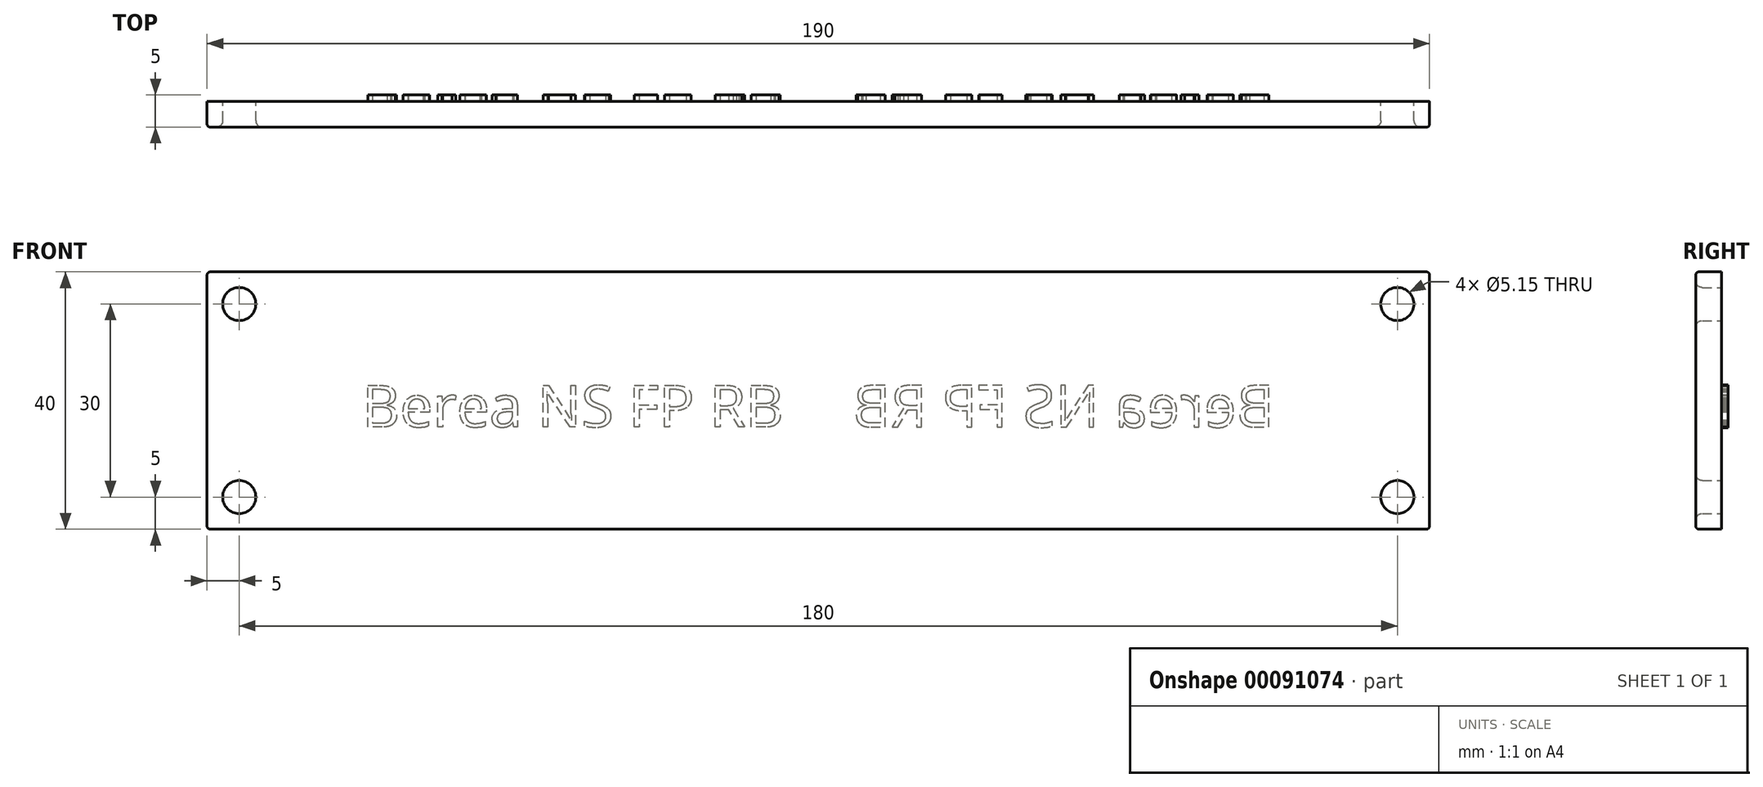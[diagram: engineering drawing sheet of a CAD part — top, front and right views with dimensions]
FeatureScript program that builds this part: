
annotation { "Feature Type Name" : "Feature", "Feature Type Description" : "" }
export const myFeature = defineFeature(function(context is Context, id is Id, definition is map)
    precondition{}
    {
        {
            var Q0;
            Q0=qCreatedBy(makeId("Front.planeOp"),FACE);
            var sketch = newSketch(context, id + "F0", { "sketchPlane" : qUnion([Q0])});
            skLineSegment(sketch, "E0.bottom", {"start": v(-95, -20) * mm, "end": v(95, -20) * mm});
            skLineSegment(sketch, "E0.top", {"start": v(-95, 20) * mm, "end": v(95, 20) * mm});
            skLineSegment(sketch, "E0.left", {"start": v(-95, -20) * mm, "end": v(-95, 20) * mm});
            skLineSegment(sketch, "E0.right", {"start": v(95, -20) * mm, "end": v(95, 20) * mm});
            skPoint(sketch, "E0.middle", {"position": v(0, 0) * mm});
            skCircle(sketch, "E1", {"center": v(-90, 15) * mm, "radius": 2.58 * mm});
            skPoint(sketch, "E2.start.orphan", {"position": v(-95, 0) * mm});
            skPoint(sketch, "E3.orphan", {"position": v(0, 20) * mm});
            skPoint(sketch, "E4.end.orphan", {"position": v(0, -20) * mm});
            skLineSegment(sketch, "E5", {"start": v(-95, 0) * mm, "end": v(0, 0) * mm, "construction": true});
            skLineSegment(sketch, "E6", {"start": v(0, 20) * mm, "end": v(0, -20) * mm, "construction": true});
            skCircle(sketch, "E7.MirrorC", {"center": v(-90, -15) * mm, "radius": 2.58 * mm});
            skCircle(sketch, "E8.MirrorC", {"center": v(90, 15) * mm, "radius": 2.58 * mm});
            skCircle(sketch, "E9.MirrorC", {"center": v(90, -15) * mm, "radius": 2.58 * mm});
            skSolve(sketch);
        }
        {
            var Q0;
            Q0=makeQuery(id+"F0.imprint","IMPRINT",FACE,{"disambiguationData":[TD([[makeQuery(id+"F0.imprint","IMPRINT",EDGE,{"derivedFrom":sQuery(id+"F0.wireOp",EDGE,"E0.bottom")}),1.0]])]});
            extrude(context, id + "F1", {"entities" : qUnion([Q0]), "depth" : 4 * mm});
        }
        {
            var Q0;
            Q0=makeQuery(id+"F1.opExtrude","CAP_EDGE",EDGE,{"disambiguationData":[OSD([sQuery(id+"F0.wireOp",EDGE,"E1")])],"isStart":false});
            var Q1;
            Q1=makeQuery(id+"F1.opExtrude","CAP_EDGE",EDGE,{"disambiguationData":[OSD([sQuery(id+"F0.wireOp",EDGE,"f5b72a5b-8583-449a-bdbf-9ac5a681e1fd0.MirrorC")])],"isStart":false});
            var Q2;
            Q2=makeQuery(id+"F1.opExtrude","CAP_EDGE",EDGE,{"disambiguationData":[OSD([sQuery(id+"F0.wireOp",EDGE,"2623e306-60f4-4522-aa65-1e3e8c2cf5b60.MirrorC")])],"isStart":false});
            var Q3;
            Q3=makeQuery(id+"F1.opExtrude","CAP_EDGE",EDGE,{"disambiguationData":[OSD([sQuery(id+"F0.wireOp",EDGE,"be81a34d-1d50-4ce7-a7a8-4484a1701fac0.MirrorC")])],"isStart":false});
            var Q4;
            Q4=makeQuery(id+"F1.opExtrude","CAP_EDGE",EDGE,{"disambiguationData":[OSD([sQuery(id+"F0.wireOp",EDGE,"E7.MirrorC")])],"isStart":false});
            var Q5;
            Q5=makeQuery(id+"F1.opExtrude","CAP_EDGE",EDGE,{"disambiguationData":[OSD([sQuery(id+"F0.wireOp",EDGE,"E8.MirrorC")])],"isStart":false});
            var Q6;
            Q6=makeQuery(id+"F1.opExtrude","CAP_EDGE",EDGE,{"disambiguationData":[OSD([sQuery(id+"F0.wireOp",EDGE,"E9.MirrorC")])],"isStart":false});
            fillet(context, id + "F2", {"entities" : qUnion([Q0, Q1, Q2, Q3, Q4, Q5, Q6]), "radius" : 1 * mm, "tangentPropagation" : true, "allowEdgeOverflow" : false});
        }
        {
            var Q0;
            Q0=makeQuery(id+"F1.opExtrude","CAP_EDGE",EDGE,{"disambiguationData":[OSD([sQuery(id+"F0.wireOp",EDGE,"E0.top")])],"isStart":false});
            var Q1;
            Q1=makeQuery(id+"F1.opExtrude","CAP_EDGE",EDGE,{"disambiguationData":[OSD([sQuery(id+"F0.wireOp",EDGE,"E0.left")])],"isStart":false});
            var Q2;
            Q2=makeQuery(id+"F1.opExtrude","CAP_EDGE",EDGE,{"disambiguationData":[OSD([sQuery(id+"F0.wireOp",EDGE,"E0.bottom")])],"isStart":false});
            var Q3;
            Q3=makeQuery(id+"F1.opExtrude","CAP_EDGE",EDGE,{"disambiguationData":[OSD([sQuery(id+"F0.wireOp",EDGE,"E0.right")])],"isStart":false});
            var Q4;
            Q4=makeQuery(id+"F1.opExtrude","SWEPT_EDGE",EDGE,{"disambiguationData":[OSD([sQuery(id+"F0.wireOp",EDGE,"E0.top"),sQuery(id+"F0.wireOp",EDGE,"E0.left")])]});
            var Q5;
            Q5=makeQuery(id+"F1.opExtrude","SWEPT_EDGE",EDGE,{"disambiguationData":[OSD([sQuery(id+"F0.wireOp",EDGE,"E0.bottom"),sQuery(id+"F0.wireOp",EDGE,"E0.left")])]});
            var Q6;
            Q6=makeQuery(id+"F1.opExtrude","SWEPT_EDGE",EDGE,{"disambiguationData":[OSD([sQuery(id+"F0.wireOp",EDGE,"E0.top"),sQuery(id+"F0.wireOp",EDGE,"E0.right")])]});
            var Q7;
            Q7=makeQuery(id+"F1.opExtrude","SWEPT_EDGE",EDGE,{"disambiguationData":[OSD([sQuery(id+"F0.wireOp",EDGE,"E0.bottom"),sQuery(id+"F0.wireOp",EDGE,"E0.right")])]});
            fillet(context, id + "F3", {"entities" : qUnion([Q0, Q1, Q2, Q3, Q4, Q5, Q6, Q7]), "radius" : .5 * mm, "tangentPropagation" : true, "allowEdgeOverflow" : false});
        }
        {
            var Q0;
            Q0=makeQuery(id+"F1.opExtrude","CAP_FACE",FACE,{"disambiguationData":[OSD([sQuery(id+"F0.wireOp",EDGE,"E0.bottom"),sQuery(id+"F0.wireOp",EDGE,"E0.top"),sQuery(id+"F0.wireOp",EDGE,"E0.left"),sQuery(id+"F0.wireOp",EDGE,"E0.right"),sQuery(id+"F0.wireOp",EDGE,"E1"),sQuery(id+"F0.wireOp",EDGE,"E7.MirrorC"),sQuery(id+"F0.wireOp",EDGE,"E8.MirrorC"),sQuery(id+"F0.wireOp",EDGE,"E9.MirrorC")])],"isStart":true});
            var sketch = newSketch(context, id + "F4", { "sketchPlane" : qUnion([Q0])});
            skText(sketch, "E10", { "text": "Berea NS FP RB\n", "fontName": "OpenSans-Regular.ttf"});
            skLineSegment(sketch, "E11", {"start": v(0, 20) * mm, "end": v(0, -20) * mm, "construction": true});
            const initialGuessF4  = {"E10": [-0.07092, -0.00413, 1, 0, 0.00655]};
            skSetInitialGuess(sketch, initialGuessF4);
            skSolve(sketch);
        }
        {
            var Q0;
            Q0=qSketchRegion(id+"F4",true);
            extrude(context, id + "F5", {"entities" : qUnion([Q0]), "operationType" : NewBodyOperationType.ADD, "flatOperationType" : FlatOperationType.REMOVE, "offsetDistance" : 25 * mm, "depth" : 1 * mm, "domain" : OperationDomain.MODEL});
        }
        {
            var Q0;
            Q0=makeQuery(id+"F1.opExtrude","SWEPT_BODY",BODY,{"disambiguationData":[OSD([sQuery(id+"F0.wireOp",EDGE,"E0.bottom"),sQuery(id+"F0.wireOp",EDGE,"E0.top"),sQuery(id+"F0.wireOp",EDGE,"E0.left"),sQuery(id+"F0.wireOp",EDGE,"E0.right"),sQuery(id+"F0.wireOp",EDGE,"E1"),sQuery(id+"F0.wireOp",EDGE,"E7.MirrorC"),sQuery(id+"F0.wireOp",EDGE,"E8.MirrorC"),sQuery(id+"F0.wireOp",EDGE,"E9.MirrorC")])]});
            var Q1;
            Q1=makeQuery(id+"F5.opExtrude","SWEPT_FACE",FACE,{"disambiguationData":[OSD([sQuery(id+"F4.wireOp",EDGE,"E10.sketch_text.stroke-94")])]});
            var Q2;
            Q2=makeQuery(id+"F5.opExtrude","SWEPT_FACE",FACE,{"disambiguationData":[OSD([sQuery(id+"F4.wireOp",EDGE,"E10.sketch_text.stroke-169")])]});
            var Q3;
            Q3=makeQuery(id+"F5.opExtrude","SWEPT_FACE",FACE,{"disambiguationData":[OSD([sQuery(id+"F4.wireOp",EDGE,"E10.sketch_text.stroke-185")])]});
            var Q4;
            Q4=makeQuery(id+"F5.opExtrude","SWEPT_FACE",FACE,{"disambiguationData":[OSD([sQuery(id+"F4.wireOp",EDGE,"E10.sketch_text.stroke-125")])]});
            var Q5;
            Q5=makeQuery(id+"F5.opExtrude","SWEPT_FACE",FACE,{"disambiguationData":[OSD([sQuery(id+"F4.wireOp",EDGE,"E10.sketch_text.stroke-155")])]});
            var Q6;
            Q6=makeQuery(id+"F5.opExtrude","SWEPT_FACE",FACE,{"disambiguationData":[OSD([sQuery(id+"F4.wireOp",EDGE,"E10.sketch_text.stroke-65")])]});
            var Q7;
            Q7=makeQuery(id+"F5.opExtrude","SWEPT_FACE",FACE,{"disambiguationData":[OSD([sQuery(id+"F4.wireOp",EDGE,"E10.sketch_text.stroke-81")])]});
            var Q8;
            Q8=makeQuery(id+"F5.opExtrude","SWEPT_FACE",FACE,{"disambiguationData":[OSD([sQuery(id+"F4.wireOp",EDGE,"E10.sketch_text.stroke-67")])]});
            var Q9;
            Q9=makeQuery(id+"F5.opExtrude","SWEPT_FACE",FACE,{"disambiguationData":[OSD([sQuery(id+"F4.wireOp",EDGE,"E10.sketch_text.stroke-99")])]});
            var Q10;
            Q10=makeQuery(id+"F5.opExtrude","SWEPT_FACE",FACE,{"disambiguationData":[OSD([sQuery(id+"F4.wireOp",EDGE,"E10.sketch_text.stroke-127")])]});
            var Q11;
            Q11=makeQuery(id+"F5.opExtrude","SWEPT_FACE",FACE,{"disambiguationData":[OSD([sQuery(id+"F4.wireOp",EDGE,"E10.sketch_text.stroke-10")])]});
            var Q12;
            Q12=makeQuery(id+"F5.opExtrude","CAP_FACE",FACE,{"disambiguationData":[OSD([sQuery(id+"F4.wireOp",EDGE,"E10.sketch_text.stroke-9"),sQuery(id+"F4.wireOp",EDGE,"E10.sketch_text.stroke-10"),sQuery(id+"F4.wireOp",EDGE,"E10.sketch_text.stroke-11"),sQuery(id+"F4.wireOp",EDGE,"E10.sketch_text.stroke-12")])],"isStart":false});
            var Q13;
            Q13=makeQuery(id+"F5.opExtrude","SWEPT_FACE",FACE,{"disambiguationData":[OSD([sQuery(id+"F4.wireOp",EDGE,"E10.sketch_text.stroke-154")])]});
            var Q14;
            Q14=makeQuery(id+"F5.opExtrude","SWEPT_FACE",FACE,{"disambiguationData":[OSD([sQuery(id+"F4.wireOp",EDGE,"E10.sketch_text.stroke-1")])]});
            var Q15;
            Q15=makeQuery(id+"F5.opExtrude","CAP_FACE",FACE,{"disambiguationData":[OSD([sQuery(id+"F4.wireOp",EDGE,"E10.sketch_text.stroke-124"),sQuery(id+"F4.wireOp",EDGE,"E10.sketch_text.stroke-125"),sQuery(id+"F4.wireOp",EDGE,"E10.sketch_text.stroke-126"),sQuery(id+"F4.wireOp",EDGE,"E10.sketch_text.stroke-127"),sQuery(id+"F4.wireOp",EDGE,"E10.sketch_text.stroke-128"),sQuery(id+"F4.wireOp",EDGE,"E10.sketch_text.stroke-129"),sQuery(id+"F4.wireOp",EDGE,"E10.sketch_text.stroke-130"),sQuery(id+"F4.wireOp",EDGE,"E10.sketch_text.stroke-131"),sQuery(id+"F4.wireOp",EDGE,"E10.sketch_text.stroke-132"),sQuery(id+"F4.wireOp",EDGE,"E10.sketch_text.stroke-133"),sQuery(id+"F4.wireOp",EDGE,"E10.sketch_text.stroke-134"),sQuery(id+"F4.wireOp",EDGE,"E10.sketch_text.stroke-135"),sQuery(id+"F4.wireOp",EDGE,"E10.sketch_text.stroke-136"),sQuery(id+"F4.wireOp",EDGE,"E10.sketch_text.stroke-137"),sQuery(id+"F4.wireOp",EDGE,"E10.sketch_text.stroke-138")])],"isStart":false});
            var Q16;
            Q16=makeQuery(id+"F5.opExtrude","CAP_FACE",FACE,{"disambiguationData":[OSD([sQuery(id+"F4.wireOp",EDGE,"E10.sketch_text.stroke-34"),sQuery(id+"F4.wireOp",EDGE,"E10.sketch_text.stroke-35"),sQuery(id+"F4.wireOp",EDGE,"E10.sketch_text.stroke-36"),sQuery(id+"F4.wireOp",EDGE,"E10.sketch_text.stroke-37"),sQuery(id+"F4.wireOp",EDGE,"E10.sketch_text.stroke-38"),sQuery(id+"F4.wireOp",EDGE,"E10.sketch_text.stroke-39"),sQuery(id+"F4.wireOp",EDGE,"E10.sketch_text.stroke-40"),sQuery(id+"F4.wireOp",EDGE,"E10.sketch_text.stroke-41"),sQuery(id+"F4.wireOp",EDGE,"E10.sketch_text.stroke-42"),sQuery(id+"F4.wireOp",EDGE,"E10.sketch_text.stroke-43"),sQuery(id+"F4.wireOp",EDGE,"E10.sketch_text.stroke-44"),sQuery(id+"F4.wireOp",EDGE,"E10.sketch_text.stroke-45"),sQuery(id+"F4.wireOp",EDGE,"E10.sketch_text.stroke-46"),sQuery(id+"F4.wireOp",EDGE,"E10.sketch_text.stroke-47"),sQuery(id+"F4.wireOp",EDGE,"E10.sketch_text.stroke-48"),sQuery(id+"F4.wireOp",EDGE,"E10.sketch_text.stroke-49"),sQuery(id+"F4.wireOp",EDGE,"E10.sketch_text.stroke-50"),sQuery(id+"F4.wireOp",EDGE,"E10.sketch_text.stroke-51"),sQuery(id+"F4.wireOp",EDGE,"E10.sketch_text.stroke-52"),sQuery(id+"F4.wireOp",EDGE,"E10.sketch_text.stroke-53"),sQuery(id+"F4.wireOp",EDGE,"E10.sketch_text.stroke-54"),sQuery(id+"F4.wireOp",EDGE,"E10.sketch_text.stroke-55"),sQuery(id+"F4.wireOp",EDGE,"E10.sketch_text.stroke-56"),sQuery(id+"F4.wireOp",EDGE,"E10.sketch_text.stroke-57"),sQuery(id+"F4.wireOp",EDGE,"E10.sketch_text.stroke-58"),sQuery(id+"F4.wireOp",EDGE,"E10.sketch_text.stroke-59"),sQuery(id+"F4.wireOp",EDGE,"E10.sketch_text.stroke-60")])],"isStart":false});
            var Q17;
            Q17=makeQuery(id+"F5.opExtrude","SWEPT_FACE",FACE,{"disambiguationData":[OSD([sQuery(id+"F4.wireOp",EDGE,"E10.sketch_text.stroke-50")])]});
            var Q18;
            Q18=makeQuery(id+"F5.opExtrude","SWEPT_FACE",FACE,{"disambiguationData":[OSD([sQuery(id+"F4.wireOp",EDGE,"E10.sketch_text.stroke-2")])]});
            var Q19;
            Q19=makeQuery(id+"F5.opExtrude","SWEPT_FACE",FACE,{"disambiguationData":[OSD([sQuery(id+"F4.wireOp",EDGE,"E10.sketch_text.stroke-3")])]});
            var Q20;
            Q20=makeQuery(id+"F5.opExtrude","SWEPT_FACE",FACE,{"disambiguationData":[OSD([sQuery(id+"F4.wireOp",EDGE,"E10.sketch_text.stroke-5")])]});
            var Q21;
            Q21=makeQuery(id+"F5.opExtrude","SWEPT_FACE",FACE,{"disambiguationData":[OSD([sQuery(id+"F4.wireOp",EDGE,"E10.sketch_text.stroke-8")])]});
            var Q22;
            Q22=makeQuery(id+"F5.opExtrude","SWEPT_FACE",FACE,{"disambiguationData":[OSD([sQuery(id+"F4.wireOp",EDGE,"E10.sketch_text.stroke-98")])]});
            var Q23;
            Q23=makeQuery(id+"F5.opExtrude","SWEPT_FACE",FACE,{"disambiguationData":[OSD([sQuery(id+"F4.wireOp",EDGE,"E10.sketch_text.stroke-66")])]});
            var Q24;
            Q24=makeQuery(id+"F5.opExtrude","SWEPT_FACE",FACE,{"disambiguationData":[OSD([sQuery(id+"F4.wireOp",EDGE,"E10.sketch_text.stroke-153")])]});
            var Q25;
            Q25=makeQuery(id+"F5.opExtrude","SWEPT_FACE",FACE,{"disambiguationData":[OSD([sQuery(id+"F4.wireOp",EDGE,"E10.sketch_text.stroke-126")])]});
            var Q26;
            Q26=makeQuery(id+"F5.opExtrude","SWEPT_FACE",FACE,{"disambiguationData":[OSD([sQuery(id+"F4.wireOp",EDGE,"E10.sketch_text.stroke-183")])]});
            var Q27;
            Q27=makeQuery(id+"F5.opExtrude","SWEPT_FACE",FACE,{"disambiguationData":[OSD([sQuery(id+"F4.wireOp",EDGE,"E10.sketch_text.stroke-109")])]});
            var Q28;
            Q28=makeQuery(id+"F5.opExtrude","SWEPT_FACE",FACE,{"disambiguationData":[OSD([sQuery(id+"F4.wireOp",EDGE,"E10.sketch_text.stroke-186")])]});
            var Q29;
            Q29=makeQuery(id+"F5.opExtrude","SWEPT_FACE",FACE,{"disambiguationData":[OSD([sQuery(id+"F4.wireOp",EDGE,"E10.sketch_text.stroke-79")])]});
            var Q30;
            Q30=makeQuery(id+"F5.opExtrude","SWEPT_FACE",FACE,{"disambiguationData":[OSD([sQuery(id+"F4.wireOp",EDGE,"E10.sketch_text.stroke-110")])]});
            var Q31;
            Q31=makeQuery(id+"F5.opExtrude","SWEPT_FACE",FACE,{"disambiguationData":[OSD([sQuery(id+"F4.wireOp",EDGE,"E10.sketch_text.stroke-38")])]});
            var Q32;
            Q32=makeQuery(id+"F5.opExtrude","SWEPT_FACE",FACE,{"disambiguationData":[OSD([sQuery(id+"F4.wireOp",EDGE,"E10.sketch_text.stroke-24")])]});
            var Q33;
            Q33=makeQuery(id+"F5.opExtrude","SWEPT_FACE",FACE,{"disambiguationData":[OSD([sQuery(id+"F4.wireOp",EDGE,"E10.sketch_text.stroke-12")])]});
            var Q34;
            Q34=makeQuery(id+"F5.opExtrude","SWEPT_FACE",FACE,{"disambiguationData":[OSD([sQuery(id+"F4.wireOp",EDGE,"E10.sketch_text.stroke-100")])]});
            var Q35;
            Q35=makeQuery(id+"F5.opExtrude","SWEPT_FACE",FACE,{"disambiguationData":[OSD([sQuery(id+"F4.wireOp",EDGE,"E10.sketch_text.stroke-158")])]});
            var Q36;
            Q36=makeQuery(id+"F5.opExtrude","SWEPT_FACE",FACE,{"disambiguationData":[OSD([sQuery(id+"F4.wireOp",EDGE,"E10.sketch_text.stroke-142")])]});
            var Q37;
            Q37=makeQuery(id+"F5.opExtrude","SWEPT_FACE",FACE,{"disambiguationData":[OSD([sQuery(id+"F4.wireOp",EDGE,"E10.sketch_text.stroke-54")])]});
            var Q38;
            Q38=makeQuery(id+"F5.opExtrude","SWEPT_FACE",FACE,{"disambiguationData":[OSD([sQuery(id+"F4.wireOp",EDGE,"E10.sketch_text.stroke-25")])]});
            var Q39;
            Q39=makeQuery(id+"F5.opExtrude","SWEPT_FACE",FACE,{"disambiguationData":[OSD([sQuery(id+"F4.wireOp",EDGE,"E10.sketch_text.stroke-101")])]});
            var Q40;
            Q40=makeQuery(id+"F5.opExtrude","SWEPT_FACE",FACE,{"disambiguationData":[OSD([sQuery(id+"F4.wireOp",EDGE,"E10.sketch_text.stroke-69")])]});
            var Q41;
            Q41=makeQuery(id+"F5.opExtrude","SWEPT_FACE",FACE,{"disambiguationData":[OSD([sQuery(id+"F4.wireOp",EDGE,"E10.sketch_text.stroke-159")])]});
            var Q42;
            Q42=makeQuery(id+"F5.opExtrude","SWEPT_FACE",FACE,{"disambiguationData":[OSD([sQuery(id+"F4.wireOp",EDGE,"E10.sketch_text.stroke-85")])]});
            var Q43;
            Q43=makeQuery(id+"F5.opExtrude","SWEPT_FACE",FACE,{"disambiguationData":[OSD([sQuery(id+"F4.wireOp",EDGE,"E10.sketch_text.stroke-173")])]});
            var Q44;
            Q44=makeQuery(id+"F5.opExtrude","SWEPT_FACE",FACE,{"disambiguationData":[OSD([sQuery(id+"F4.wireOp",EDGE,"E10.sketch_text.stroke-40")])]});
            var Q45;
            Q45=makeQuery(id+"F5.opExtrude","SWEPT_FACE",FACE,{"disambiguationData":[OSD([sQuery(id+"F4.wireOp",EDGE,"E10.sketch_text.stroke-102")])]});
            var Q46;
            Q46=makeQuery(id+"F5.opExtrude","SWEPT_FACE",FACE,{"disambiguationData":[OSD([sQuery(id+"F4.wireOp",EDGE,"E10.sketch_text.stroke-86")])]});
            var Q47;
            Q47=makeQuery(id+"F5.opExtrude","SWEPT_FACE",FACE,{"disambiguationData":[OSD([sQuery(id+"F4.wireOp",EDGE,"E10.sketch_text.stroke-130")])]});
            var Q48;
            Q48=makeQuery(id+"F5.opExtrude","SWEPT_FACE",FACE,{"disambiguationData":[OSD([sQuery(id+"F4.wireOp",EDGE,"E10.sketch_text.stroke-103")])]});
            var Q49;
            Q49=makeQuery(id+"F5.opExtrude","SWEPT_FACE",FACE,{"disambiguationData":[OSD([sQuery(id+"F4.wireOp",EDGE,"E10.sketch_text.stroke-87")])]});
            var Q50;
            Q50=makeQuery(id+"F5.opExtrude","SWEPT_FACE",FACE,{"disambiguationData":[OSD([sQuery(id+"F4.wireOp",EDGE,"E10.sketch_text.stroke-145")])]});
            var Q51;
            Q51=makeQuery(id+"F5.opExtrude","SWEPT_FACE",FACE,{"disambiguationData":[OSD([sQuery(id+"F4.wireOp",EDGE,"E10.sketch_text.stroke-131")])]});
            var Q52;
            Q52=makeQuery(id+"F5.opExtrude","SWEPT_FACE",FACE,{"disambiguationData":[OSD([sQuery(id+"F4.wireOp",EDGE,"E10.sketch_text.stroke-28")])]});
            var Q53;
            Q53=makeQuery(id+"F5.opExtrude","SWEPT_FACE",FACE,{"disambiguationData":[OSD([sQuery(id+"F4.wireOp",EDGE,"E10.sketch_text.stroke-14")])]});
            var Q54;
            Q54=makeQuery(id+"F5.opExtrude","SWEPT_FACE",FACE,{"disambiguationData":[OSD([sQuery(id+"F4.wireOp",EDGE,"E10.sketch_text.stroke-88")])]});
            var Q55;
            Q55=makeQuery(id+"F5.opExtrude","SWEPT_FACE",FACE,{"disambiguationData":[OSD([sQuery(id+"F4.wireOp",EDGE,"E10.sketch_text.stroke-162")])]});
            var Q56;
            Q56=makeQuery(id+"F5.opExtrude","SWEPT_FACE",FACE,{"disambiguationData":[OSD([sQuery(id+"F4.wireOp",EDGE,"E10.sketch_text.stroke-176")])]});
            var Q57;
            Q57=makeQuery(id+"F5.opExtrude","SWEPT_FACE",FACE,{"disambiguationData":[OSD([sQuery(id+"F4.wireOp",EDGE,"E10.sketch_text.stroke-73")])]});
            var Q58;
            Q58=makeQuery(id+"F5.opExtrude","SWEPT_FACE",FACE,{"disambiguationData":[OSD([sQuery(id+"F4.wireOp",EDGE,"E10.sketch_text.stroke-59")])]});
            var Q59;
            Q59=makeQuery(id+"F5.opExtrude","SWEPT_FACE",FACE,{"disambiguationData":[OSD([sQuery(id+"F4.wireOp",EDGE,"E10.sketch_text.stroke-133")])]});
            var Q60;
            Q60=makeQuery(id+"F5.opExtrude","SWEPT_FACE",FACE,{"disambiguationData":[OSD([sQuery(id+"F4.wireOp",EDGE,"E10.sketch_text.stroke-119")])]});
            var Q61;
            Q61=makeQuery(id+"F5.opExtrude","SWEPT_FACE",FACE,{"disambiguationData":[OSD([sQuery(id+"F4.wireOp",EDGE,"E10.sketch_text.stroke-74")])]});
            var Q62;
            Q62=makeQuery(id+"F5.opExtrude","SWEPT_FACE",FACE,{"disambiguationData":[OSD([sQuery(id+"F4.wireOp",EDGE,"E10.sketch_text.stroke-44")])]});
            var Q63;
            Q63=makeQuery(id+"F5.opExtrude","SWEPT_FACE",FACE,{"disambiguationData":[OSD([sQuery(id+"F4.wireOp",EDGE,"E10.sketch_text.stroke-120")])]});
            var Q64;
            Q64=makeQuery(id+"F5.opExtrude","SWEPT_FACE",FACE,{"disambiguationData":[OSD([sQuery(id+"F4.wireOp",EDGE,"E10.sketch_text.stroke-90")])]});
            var Q65;
            Q65=makeQuery(id+"F5.opExtrude","SWEPT_FACE",FACE,{"disambiguationData":[OSD([sQuery(id+"F4.wireOp",EDGE,"E10.sketch_text.stroke-178")])]});
            var Q66;
            Q66=makeQuery(id+"F5.opExtrude","SWEPT_FACE",FACE,{"disambiguationData":[OSD([sQuery(id+"F4.wireOp",EDGE,"E10.sketch_text.stroke-45")])]});
            var Q67;
            Q67=makeQuery(id+"F5.opExtrude","SWEPT_FACE",FACE,{"disambiguationData":[OSD([sQuery(id+"F4.wireOp",EDGE,"E10.sketch_text.stroke-31")])]});
            var Q68;
            Q68=makeQuery(id+"F5.opExtrude","SWEPT_FACE",FACE,{"disambiguationData":[OSD([sQuery(id+"F4.wireOp",EDGE,"E10.sketch_text.stroke-135")])]});
            var Q69;
            Q69=makeQuery(id+"F5.opExtrude","SWEPT_FACE",FACE,{"disambiguationData":[OSD([sQuery(id+"F4.wireOp",EDGE,"E10.sketch_text.stroke-179")])]});
            var Q70;
            Q70=makeQuery(id+"F5.opExtrude","SWEPT_FACE",FACE,{"disambiguationData":[OSD([sQuery(id+"F4.wireOp",EDGE,"E10.sketch_text.stroke-165")])]});
            var Q71;
            Q71=makeQuery(id+"F5.opExtrude","SWEPT_FACE",FACE,{"disambiguationData":[OSD([sQuery(id+"F4.wireOp",EDGE,"E10.sketch_text.stroke-149")])]});
            var Q72;
            Q72=makeQuery(id+"F5.opExtrude","SWEPT_FACE",FACE,{"disambiguationData":[OSD([sQuery(id+"F4.wireOp",EDGE,"E10.sketch_text.stroke-136")])]});
            var Q73;
            Q73=makeQuery(id+"F5.opExtrude","SWEPT_FACE",FACE,{"disambiguationData":[OSD([sQuery(id+"F4.wireOp",EDGE,"E10.sketch_text.stroke-122")])]});
            var Q74;
            Q74=makeQuery(id+"F5.opExtrude","SWEPT_FACE",FACE,{"disambiguationData":[OSD([sQuery(id+"F4.wireOp",EDGE,"E10.sketch_text.stroke-106")])]});
            var Q75;
            Q75=makeQuery(id+"F5.opExtrude","SWEPT_FACE",FACE,{"disambiguationData":[OSD([sQuery(id+"F4.wireOp",EDGE,"E10.sketch_text.stroke-180")])]});
            var Q76;
            Q76=makeQuery(id+"F5.opExtrude","SWEPT_FACE",FACE,{"disambiguationData":[OSD([sQuery(id+"F4.wireOp",EDGE,"E10.sketch_text.stroke-166")])]});
            var Q77;
            Q77=makeQuery(id+"F5.opExtrude","SWEPT_FACE",FACE,{"disambiguationData":[OSD([sQuery(id+"F4.wireOp",EDGE,"E10.sketch_text.stroke-150")])]});
            var Q78;
            Q78=makeQuery(id+"F5.opExtrude","SWEPT_FACE",FACE,{"disambiguationData":[OSD([sQuery(id+"F4.wireOp",EDGE,"E10.sketch_text.stroke-76")])]});
            var Q79;
            Q79=makeQuery(id+"F5.opExtrude","SWEPT_FACE",FACE,{"disambiguationData":[OSD([sQuery(id+"F4.wireOp",EDGE,"E10.sketch_text.stroke-32")])]});
            var Q80;
            Q80=makeQuery(id+"F5.opExtrude","SWEPT_FACE",FACE,{"disambiguationData":[OSD([sQuery(id+"F4.wireOp",EDGE,"E10.sketch_text.stroke-181")])]});
            var Q81;
            Q81=makeQuery(id+"F5.opExtrude","SWEPT_FACE",FACE,{"disambiguationData":[OSD([sQuery(id+"F4.wireOp",EDGE,"E10.sketch_text.stroke-47")])]});
            var Q82;
            Q82=makeQuery(id+"F5.opExtrude","SWEPT_FACE",FACE,{"disambiguationData":[OSD([sQuery(id+"F4.wireOp",EDGE,"E10.sketch_text.stroke-123")])]});
            var Q83;
            Q83=makeQuery(id+"F5.opExtrude","SWEPT_FACE",FACE,{"disambiguationData":[OSD([sQuery(id+"F4.wireOp",EDGE,"E10.sketch_text.stroke-107")])]});
            var Q84;
            Q84=makeQuery(id+"F5.opExtrude","SWEPT_FACE",FACE,{"disambiguationData":[OSD([sQuery(id+"F4.wireOp",EDGE,"E10.sketch_text.stroke-48")])]});
            var Q85;
            Q85=makeQuery(id+"F5.opExtrude","SWEPT_FACE",FACE,{"disambiguationData":[OSD([sQuery(id+"F4.wireOp",EDGE,"E10.sketch_text.stroke-124")])]});
            var Q86;
            Q86=makeQuery(id+"F5.opExtrude","SWEPT_FACE",FACE,{"disambiguationData":[OSD([sQuery(id+"F4.wireOp",EDGE,"E10.sketch_text.stroke-108")])]});
            var Q87;
            Q87=makeQuery(id+"F5.opExtrude","CAP_FACE",FACE,{"disambiguationData":[OSD([sQuery(id+"F4.wireOp",EDGE,"E10.sketch_text.stroke-139"),sQuery(id+"F4.wireOp",EDGE,"E10.sketch_text.stroke-140"),sQuery(id+"F4.wireOp",EDGE,"E10.sketch_text.stroke-141"),sQuery(id+"F4.wireOp",EDGE,"E10.sketch_text.stroke-142"),sQuery(id+"F4.wireOp",EDGE,"E10.sketch_text.stroke-143"),sQuery(id+"F4.wireOp",EDGE,"E10.sketch_text.stroke-144"),sQuery(id+"F4.wireOp",EDGE,"E10.sketch_text.stroke-145"),sQuery(id+"F4.wireOp",EDGE,"E10.sketch_text.stroke-146"),sQuery(id+"F4.wireOp",EDGE,"E10.sketch_text.stroke-147"),sQuery(id+"F4.wireOp",EDGE,"E10.sketch_text.stroke-148"),sQuery(id+"F4.wireOp",EDGE,"E10.sketch_text.stroke-149"),sQuery(id+"F4.wireOp",EDGE,"E10.sketch_text.stroke-150"),sQuery(id+"F4.wireOp",EDGE,"E10.sketch_text.stroke-151"),sQuery(id+"F4.wireOp",EDGE,"E10.sketch_text.stroke-152"),sQuery(id+"F4.wireOp",EDGE,"E10.sketch_text.stroke-153"),sQuery(id+"F4.wireOp",EDGE,"E10.sketch_text.stroke-154"),sQuery(id+"F4.wireOp",EDGE,"E10.sketch_text.stroke-155"),sQuery(id+"F4.wireOp",EDGE,"E10.sketch_text.stroke-156"),sQuery(id+"F4.wireOp",EDGE,"E10.sketch_text.stroke-157"),sQuery(id+"F4.wireOp",EDGE,"E10.sketch_text.stroke-158"),sQuery(id+"F4.wireOp",EDGE,"E10.sketch_text.stroke-159"),sQuery(id+"F4.wireOp",EDGE,"E10.sketch_text.stroke-160"),sQuery(id+"F4.wireOp",EDGE,"E10.sketch_text.stroke-161"),sQuery(id+"F4.wireOp",EDGE,"E10.sketch_text.stroke-162"),sQuery(id+"F4.wireOp",EDGE,"E10.sketch_text.stroke-163"),sQuery(id+"F4.wireOp",EDGE,"E10.sketch_text.stroke-164"),sQuery(id+"F4.wireOp",EDGE,"E10.sketch_text.stroke-165")])],"isStart":false});
            var Q88;
            Q88=makeQuery(id+"F5.opExtrude","CAP_FACE",FACE,{"disambiguationData":[OSD([sQuery(id+"F4.wireOp",EDGE,"E10.sketch_text.stroke-21"),sQuery(id+"F4.wireOp",EDGE,"E10.sketch_text.stroke-22"),sQuery(id+"F4.wireOp",EDGE,"E10.sketch_text.stroke-23"),sQuery(id+"F4.wireOp",EDGE,"E10.sketch_text.stroke-24"),sQuery(id+"F4.wireOp",EDGE,"E10.sketch_text.stroke-25"),sQuery(id+"F4.wireOp",EDGE,"E10.sketch_text.stroke-26"),sQuery(id+"F4.wireOp",EDGE,"E10.sketch_text.stroke-27"),sQuery(id+"F4.wireOp",EDGE,"E10.sketch_text.stroke-28"),sQuery(id+"F4.wireOp",EDGE,"E10.sketch_text.stroke-29"),sQuery(id+"F4.wireOp",EDGE,"E10.sketch_text.stroke-30"),sQuery(id+"F4.wireOp",EDGE,"E10.sketch_text.stroke-31"),sQuery(id+"F4.wireOp",EDGE,"E10.sketch_text.stroke-32"),sQuery(id+"F4.wireOp",EDGE,"E10.sketch_text.stroke-33")])],"isStart":false});
            var Q89;
            Q89=makeQuery(id+"F5.opExtrude","SWEPT_FACE",FACE,{"disambiguationData":[OSD([sQuery(id+"F4.wireOp",EDGE,"E10.sketch_text.stroke-113")])]});
            var Q90;
            Q90=makeQuery(id+"F5.opExtrude","SWEPT_FACE",FACE,{"disambiguationData":[OSD([sQuery(id+"F4.wireOp",EDGE,"E10.sketch_text.stroke-37")])]});
            var Q91;
            Q91=makeQuery(id+"F5.opExtrude","SWEPT_FACE",FACE,{"disambiguationData":[OSD([sQuery(id+"F4.wireOp",EDGE,"E10.sketch_text.stroke-187")])]});
            var Q92;
            Q92=makeQuery(id+"F5.opExtrude","SWEPT_FACE",FACE,{"disambiguationData":[OSD([sQuery(id+"F4.wireOp",EDGE,"E10.sketch_text.stroke-0")])]});
            var Q93;
            Q93=makeQuery(id+"F5.opExtrude","SWEPT_FACE",FACE,{"disambiguationData":[OSD([sQuery(id+"F4.wireOp",EDGE,"E10.sketch_text.stroke-4")])]});
            var Q94;
            Q94=makeQuery(id+"F5.opExtrude","SWEPT_FACE",FACE,{"disambiguationData":[OSD([sQuery(id+"F4.wireOp",EDGE,"E10.sketch_text.stroke-82")])]});
            var Q95;
            Q95=makeQuery(id+"F5.opExtrude","SWEPT_FACE",FACE,{"disambiguationData":[OSD([sQuery(id+"F4.wireOp",EDGE,"E10.sketch_text.stroke-52")])]});
            var Q96;
            Q96=makeQuery(id+"F5.opExtrude","SWEPT_FACE",FACE,{"disambiguationData":[OSD([sQuery(id+"F4.wireOp",EDGE,"E10.sketch_text.stroke-49")])]});
            var Q97;
            Q97=makeQuery(id+"F5.opExtrude","SWEPT_FACE",FACE,{"disambiguationData":[OSD([sQuery(id+"F4.wireOp",EDGE,"E10.sketch_text.stroke-63")])]});
            var Q98;
            Q98=makeQuery(id+"F5.opExtrude","SWEPT_FACE",FACE,{"disambiguationData":[OSD([sQuery(id+"F4.wireOp",EDGE,"E10.sketch_text.stroke-21")])]});
            var Q99;
            Q99=makeQuery(id+"F5.opExtrude","SWEPT_FACE",FACE,{"disambiguationData":[OSD([sQuery(id+"F4.wireOp",EDGE,"E10.sketch_text.stroke-128")])]});
            var Q100;
            Q100=makeQuery(id+"F5.opExtrude","SWEPT_FACE",FACE,{"disambiguationData":[OSD([sQuery(id+"F4.wireOp",EDGE,"E10.sketch_text.stroke-55")])]});
            var Q101;
            Q101=makeQuery(id+"F5.opExtrude","SWEPT_FACE",FACE,{"disambiguationData":[OSD([sQuery(id+"F4.wireOp",EDGE,"E10.sketch_text.stroke-26")])]});
            var Q102;
            Q102=makeQuery(id+"F5.opExtrude","SWEPT_FACE",FACE,{"disambiguationData":[OSD([sQuery(id+"F4.wireOp",EDGE,"E10.sketch_text.stroke-174")])]});
            var Q103;
            Q103=makeQuery(id+"F5.opExtrude","SWEPT_FACE",FACE,{"disambiguationData":[OSD([sQuery(id+"F4.wireOp",EDGE,"E10.sketch_text.stroke-104")])]});
            var Q104;
            Q104=makeQuery(id+"F5.opExtrude","SWEPT_FACE",FACE,{"disambiguationData":[OSD([sQuery(id+"F4.wireOp",EDGE,"E10.sketch_text.stroke-72")])]});
            var Q105;
            Q105=makeQuery(id+"F5.opExtrude","SWEPT_FACE",FACE,{"disambiguationData":[OSD([sQuery(id+"F4.wireOp",EDGE,"E10.sketch_text.stroke-132")])]});
            var Q106;
            Q106=makeQuery(id+"F5.opExtrude","SWEPT_FACE",FACE,{"disambiguationData":[OSD([sQuery(id+"F4.wireOp",EDGE,"E10.sketch_text.stroke-43")])]});
            var Q107;
            Q107=makeQuery(id+"F5.opExtrude","SWEPT_FACE",FACE,{"disambiguationData":[OSD([sQuery(id+"F4.wireOp",EDGE,"E10.sketch_text.stroke-15")])]});
            var Q108;
            Q108=makeQuery(id+"F5.opExtrude","SWEPT_FACE",FACE,{"disambiguationData":[OSD([sQuery(id+"F4.wireOp",EDGE,"E10.sketch_text.stroke-89")])]});
            var Q109;
            Q109=makeQuery(id+"F5.opExtrude","SWEPT_FACE",FACE,{"disambiguationData":[OSD([sQuery(id+"F4.wireOp",EDGE,"E10.sketch_text.stroke-163")])]});
            var Q110;
            Q110=makeQuery(id+"F5.opExtrude","SWEPT_FACE",FACE,{"disambiguationData":[OSD([sQuery(id+"F4.wireOp",EDGE,"E10.sketch_text.stroke-30")])]});
            var Q111;
            Q111=makeQuery(id+"F5.opExtrude","SWEPT_FACE",FACE,{"disambiguationData":[OSD([sQuery(id+"F4.wireOp",EDGE,"E10.sketch_text.stroke-134")])]});
            var Q112;
            Q112=makeQuery(id+"F5.opExtrude","SWEPT_FACE",FACE,{"disambiguationData":[OSD([sQuery(id+"F4.wireOp",EDGE,"E10.sketch_text.stroke-121")])]});
            var Q113;
            Q113=makeQuery(id+"F5.opExtrude","CAP_FACE",FACE,{"disambiguationData":[OSD([sQuery(id+"F4.wireOp",EDGE,"E10.sketch_text.stroke-105"),sQuery(id+"F4.wireOp",EDGE,"E10.sketch_text.stroke-106"),sQuery(id+"F4.wireOp",EDGE,"E10.sketch_text.stroke-107"),sQuery(id+"F4.wireOp",EDGE,"E10.sketch_text.stroke-108"),sQuery(id+"F4.wireOp",EDGE,"E10.sketch_text.stroke-109"),sQuery(id+"F4.wireOp",EDGE,"E10.sketch_text.stroke-110"),sQuery(id+"F4.wireOp",EDGE,"E10.sketch_text.stroke-111"),sQuery(id+"F4.wireOp",EDGE,"E10.sketch_text.stroke-112"),sQuery(id+"F4.wireOp",EDGE,"E10.sketch_text.stroke-113"),sQuery(id+"F4.wireOp",EDGE,"E10.sketch_text.stroke-114"),sQuery(id+"F4.wireOp",EDGE,"E10.sketch_text.stroke-115"),sQuery(id+"F4.wireOp",EDGE,"E10.sketch_text.stroke-116"),sQuery(id+"F4.wireOp",EDGE,"E10.sketch_text.stroke-117"),sQuery(id+"F4.wireOp",EDGE,"E10.sketch_text.stroke-118"),sQuery(id+"F4.wireOp",EDGE,"E10.sketch_text.stroke-119"),sQuery(id+"F4.wireOp",EDGE,"E10.sketch_text.stroke-120"),sQuery(id+"F4.wireOp",EDGE,"E10.sketch_text.stroke-121"),sQuery(id+"F4.wireOp",EDGE,"E10.sketch_text.stroke-122"),sQuery(id+"F4.wireOp",EDGE,"E10.sketch_text.stroke-123")])],"isStart":false});
            var Q114;
            Q114=makeQuery(id+"F5.opExtrude","SWEPT_FACE",FACE,{"disambiguationData":[OSD([sQuery(id+"F4.wireOp",EDGE,"E10.sketch_text.stroke-92")])]});
            var Q115;
            Q115=makeQuery(id+"F5.opExtrude","SWEPT_FACE",FACE,{"disambiguationData":[OSD([sQuery(id+"F4.wireOp",EDGE,"E10.sketch_text.stroke-46")])]});
            var Q116;
            Q116=makeQuery(id+"F5.opExtrude","CAP_FACE",FACE,{"disambiguationData":[OSD([sQuery(id+"F4.wireOp",EDGE,"E10.sketch_text.stroke-61"),sQuery(id+"F4.wireOp",EDGE,"E10.sketch_text.stroke-62"),sQuery(id+"F4.wireOp",EDGE,"E10.sketch_text.stroke-63"),sQuery(id+"F4.wireOp",EDGE,"E10.sketch_text.stroke-64"),sQuery(id+"F4.wireOp",EDGE,"E10.sketch_text.stroke-65"),sQuery(id+"F4.wireOp",EDGE,"E10.sketch_text.stroke-66"),sQuery(id+"F4.wireOp",EDGE,"E10.sketch_text.stroke-67"),sQuery(id+"F4.wireOp",EDGE,"E10.sketch_text.stroke-68"),sQuery(id+"F4.wireOp",EDGE,"E10.sketch_text.stroke-69"),sQuery(id+"F4.wireOp",EDGE,"E10.sketch_text.stroke-70"),sQuery(id+"F4.wireOp",EDGE,"E10.sketch_text.stroke-71"),sQuery(id+"F4.wireOp",EDGE,"E10.sketch_text.stroke-72"),sQuery(id+"F4.wireOp",EDGE,"E10.sketch_text.stroke-73"),sQuery(id+"F4.wireOp",EDGE,"E10.sketch_text.stroke-74"),sQuery(id+"F4.wireOp",EDGE,"E10.sketch_text.stroke-75"),sQuery(id+"F4.wireOp",EDGE,"E10.sketch_text.stroke-76"),sQuery(id+"F4.wireOp",EDGE,"E10.sketch_text.stroke-77"),sQuery(id+"F4.wireOp",EDGE,"E10.sketch_text.stroke-78"),sQuery(id+"F4.wireOp",EDGE,"E10.sketch_text.stroke-79"),sQuery(id+"F4.wireOp",EDGE,"E10.sketch_text.stroke-80"),sQuery(id+"F4.wireOp",EDGE,"E10.sketch_text.stroke-81"),sQuery(id+"F4.wireOp",EDGE,"E10.sketch_text.stroke-82"),sQuery(id+"F4.wireOp",EDGE,"E10.sketch_text.stroke-83"),sQuery(id+"F4.wireOp",EDGE,"E10.sketch_text.stroke-84"),sQuery(id+"F4.wireOp",EDGE,"E10.sketch_text.stroke-85"),sQuery(id+"F4.wireOp",EDGE,"E10.sketch_text.stroke-86"),sQuery(id+"F4.wireOp",EDGE,"E10.sketch_text.stroke-87"),sQuery(id+"F4.wireOp",EDGE,"E10.sketch_text.stroke-88"),sQuery(id+"F4.wireOp",EDGE,"E10.sketch_text.stroke-89"),sQuery(id+"F4.wireOp",EDGE,"E10.sketch_text.stroke-90"),sQuery(id+"F4.wireOp",EDGE,"E10.sketch_text.stroke-91"),sQuery(id+"F4.wireOp",EDGE,"E10.sketch_text.stroke-92"),sQuery(id+"F4.wireOp",EDGE,"E10.sketch_text.stroke-93"),sQuery(id+"F4.wireOp",EDGE,"E10.sketch_text.stroke-94"),sQuery(id+"F4.wireOp",EDGE,"E10.sketch_text.stroke-95"),sQuery(id+"F4.wireOp",EDGE,"E10.sketch_text.stroke-96"),sQuery(id+"F4.wireOp",EDGE,"E10.sketch_text.stroke-97"),sQuery(id+"F4.wireOp",EDGE,"E10.sketch_text.stroke-98"),sQuery(id+"F4.wireOp",EDGE,"E10.sketch_text.stroke-99"),sQuery(id+"F4.wireOp",EDGE,"E10.sketch_text.stroke-100"),sQuery(id+"F4.wireOp",EDGE,"E10.sketch_text.stroke-101"),sQuery(id+"F4.wireOp",EDGE,"E10.sketch_text.stroke-102"),sQuery(id+"F4.wireOp",EDGE,"E10.sketch_text.stroke-103"),sQuery(id+"F4.wireOp",EDGE,"E10.sketch_text.stroke-104")])],"isStart":false});
            var Q117;
            Q117=makeQuery(id+"F5.opExtrude","SWEPT_FACE",FACE,{"disambiguationData":[OSD([sQuery(id+"F4.wireOp",EDGE,"E10.sketch_text.stroke-33")])]});
            var Q118;
            Q118=makeQuery(id+"F5.opExtrude","SWEPT_FACE",FACE,{"disambiguationData":[OSD([sQuery(id+"F4.wireOp",EDGE,"E10.sketch_text.stroke-93")])]});
            var Q119;
            Q119=makeQuery(id+"F5.opExtrude","SWEPT_FACE",FACE,{"disambiguationData":[OSD([sQuery(id+"F4.wireOp",EDGE,"E10.sketch_text.stroke-34")])]});
            var Q120;
            Q120=makeQuery(id+"F5.opExtrude","SWEPT_FACE",FACE,{"disambiguationData":[OSD([sQuery(id+"F4.wireOp",EDGE,"E10.sketch_text.stroke-152")])]});
            var Q121;
            Q121=makeQuery(id+"F5.opExtrude","SWEPT_FACE",FACE,{"disambiguationData":[OSD([sQuery(id+"F4.wireOp",EDGE,"E10.sketch_text.stroke-51")])]});
            var Q122;
            Q122=makeQuery(id+"F5.opExtrude","SWEPT_FACE",FACE,{"disambiguationData":[OSD([sQuery(id+"F4.wireOp",EDGE,"E10.sketch_text.stroke-6")])]});
            var Q123;
            Q123=makeQuery(id+"F5.opExtrude","SWEPT_FACE",FACE,{"disambiguationData":[OSD([sQuery(id+"F4.wireOp",EDGE,"E10.sketch_text.stroke-7")])]});
            var Q124;
            Q124=makeQuery(id+"F5.opExtrude","SWEPT_FACE",FACE,{"disambiguationData":[OSD([sQuery(id+"F4.wireOp",EDGE,"E10.sketch_text.stroke-156")])]});
            var Q125;
            Q125=makeQuery(id+"F5.opExtrude","SWEPT_FACE",FACE,{"disambiguationData":[OSD([sQuery(id+"F4.wireOp",EDGE,"E10.sketch_text.stroke-112")])]});
            var Q126;
            Q126=makeQuery(id+"F5.boolean.opBoolean","SPLIT",FACE,{"disambiguationData":[TD([makeQuery(id+"F5.opExtrude","SWEPT_FACE",FACE,{"disambiguationData":[OSD([sQuery(id+"F4.wireOp",EDGE,"E10.sketch_text.stroke-182")])]})])],"derivedFrom":makeQuery(id+"F1.opExtrude","CAP_FACE",FACE,{"disambiguationData":[OSD([sQuery(id+"F0.wireOp",EDGE,"E0.bottom"),sQuery(id+"F0.wireOp",EDGE,"E0.top"),sQuery(id+"F0.wireOp",EDGE,"E0.left"),sQuery(id+"F0.wireOp",EDGE,"E0.right"),sQuery(id+"F0.wireOp",EDGE,"E1"),sQuery(id+"F0.wireOp",EDGE,"E7.MirrorC"),sQuery(id+"F0.wireOp",EDGE,"E8.MirrorC"),sQuery(id+"F0.wireOp",EDGE,"E9.MirrorC")])],"isStart":true})});
            var Q127;
            Q127=makeQuery(id+"F5.opExtrude","SWEPT_FACE",FACE,{"disambiguationData":[OSD([sQuery(id+"F4.wireOp",EDGE,"E10.sketch_text.stroke-96")])]});
            var Q128;
            Q128=makeQuery(id+"F5.opExtrude","SWEPT_FACE",FACE,{"disambiguationData":[OSD([sQuery(id+"F4.wireOp",EDGE,"E10.sketch_text.stroke-114")])]});
            var Q129;
            Q129=makeQuery(id+"F5.opExtrude","SWEPT_FACE",FACE,{"disambiguationData":[OSD([sQuery(id+"F4.wireOp",EDGE,"E10.sketch_text.stroke-39")])]});
            var Q130;
            Q130=makeQuery(id+"F5.opExtrude","SWEPT_FACE",FACE,{"disambiguationData":[OSD([sQuery(id+"F4.wireOp",EDGE,"E10.sketch_text.stroke-13")])]});
            var Q131;
            Q131=makeQuery(id+"F5.opExtrude","SWEPT_FACE",FACE,{"disambiguationData":[OSD([sQuery(id+"F4.wireOp",EDGE,"E10.sketch_text.stroke-115")])]});
            var Q132;
            Q132=makeQuery(id+"F5.opExtrude","SWEPT_FACE",FACE,{"disambiguationData":[OSD([sQuery(id+"F4.wireOp",EDGE,"E10.sketch_text.stroke-56")])]});
            var Q133;
            Q133=makeQuery(id+"F5.opExtrude","SWEPT_FACE",FACE,{"disambiguationData":[OSD([sQuery(id+"F4.wireOp",EDGE,"E10.sketch_text.stroke-144")])]});
            var Q134;
            Q134=makeQuery(id+"F5.opExtrude","SWEPT_FACE",FACE,{"disambiguationData":[OSD([sQuery(id+"F4.wireOp",EDGE,"E10.sketch_text.stroke-190")])]});
            var Q135;
            Q135=makeQuery(id+"F5.opExtrude","SWEPT_FACE",FACE,{"disambiguationData":[OSD([sQuery(id+"F4.wireOp",EDGE,"E10.sketch_text.stroke-116")])]});
            var Q136;
            Q136=makeQuery(id+"F5.opExtrude","SWEPT_FACE",FACE,{"disambiguationData":[OSD([sQuery(id+"F4.wireOp",EDGE,"E10.sketch_text.stroke-41")])]});
            var Q137;
            Q137=makeQuery(id+"F5.opExtrude","SWEPT_FACE",FACE,{"disambiguationData":[OSD([sQuery(id+"F4.wireOp",EDGE,"E10.sketch_text.stroke-161")])]});
            var Q138;
            Q138=makeQuery(id+"F5.opExtrude","SWEPT_FACE",FACE,{"disambiguationData":[OSD([sQuery(id+"F4.wireOp",EDGE,"E10.sketch_text.stroke-146")])]});
            var Q139;
            Q139=makeQuery(id+"F5.opExtrude","SWEPT_FACE",FACE,{"disambiguationData":[OSD([sQuery(id+"F4.wireOp",EDGE,"E10.sketch_text.stroke-58")])]});
            var Q140;
            Q140=makeQuery(id+"F5.opExtrude","SWEPT_FACE",FACE,{"disambiguationData":[OSD([sQuery(id+"F4.wireOp",EDGE,"E10.sketch_text.stroke-105")])]});
            var Q141;
            Q141=makeQuery(id+"F5.opExtrude","SWEPT_FACE",FACE,{"disambiguationData":[OSD([sQuery(id+"F4.wireOp",EDGE,"E10.sketch_text.stroke-177")])]});
            var Q142;
            Q142=makeQuery(id+"F5.opExtrude","SWEPT_FACE",FACE,{"disambiguationData":[OSD([sQuery(id+"F4.wireOp",EDGE,"E10.sketch_text.stroke-77")])]});
            var Q143;
            Q143=makeQuery(id+"F5.opExtrude","SWEPT_FACE",FACE,{"disambiguationData":[OSD([sQuery(id+"F4.wireOp",EDGE,"E10.sketch_text.stroke-138")])]});
            var Q144;
            Q144=makeQuery(id+"F5.opExtrude","SWEPT_FACE",FACE,{"disambiguationData":[OSD([sQuery(id+"F4.wireOp",EDGE,"E10.sketch_text.stroke-111")])]});
            var Q145;
            Q145=makeQuery(id+"F5.opExtrude","SWEPT_FACE",FACE,{"disambiguationData":[OSD([sQuery(id+"F4.wireOp",EDGE,"E10.sketch_text.stroke-53")])]});
            var Q146;
            Q146=makeQuery(id+"F5.opExtrude","SWEPT_FACE",FACE,{"disambiguationData":[OSD([sQuery(id+"F4.wireOp",EDGE,"E10.sketch_text.stroke-141")])]});
            var Q147;
            Q147=makeQuery(id+"F5.opExtrude","SWEPT_FACE",FACE,{"disambiguationData":[OSD([sQuery(id+"F4.wireOp",EDGE,"E10.sketch_text.stroke-157")])]});
            var Q148;
            Q148=makeQuery(id+"F5.opExtrude","SWEPT_FACE",FACE,{"disambiguationData":[OSD([sQuery(id+"F4.wireOp",EDGE,"E10.sketch_text.stroke-64")])]});
            var Q149;
            Q149=makeQuery(id+"F5.boolean.opBoolean","SPLIT",FACE,{"disambiguationData":[TD([makeQuery(id+"F5.opExtrude","SWEPT_FACE",FACE,{"disambiguationData":[OSD([sQuery(id+"F4.wireOp",EDGE,"E10.sketch_text.stroke-53")])]})])],"derivedFrom":makeQuery(id+"F1.opExtrude","CAP_FACE",FACE,{"disambiguationData":[OSD([sQuery(id+"F0.wireOp",EDGE,"E0.bottom"),sQuery(id+"F0.wireOp",EDGE,"E0.top"),sQuery(id+"F0.wireOp",EDGE,"E0.left"),sQuery(id+"F0.wireOp",EDGE,"E0.right"),sQuery(id+"F0.wireOp",EDGE,"E1"),sQuery(id+"F0.wireOp",EDGE,"E7.MirrorC"),sQuery(id+"F0.wireOp",EDGE,"E8.MirrorC"),sQuery(id+"F0.wireOp",EDGE,"E9.MirrorC")])],"isStart":true})});
            var Q150;
            Q150=makeQuery(id+"F5.opExtrude","SWEPT_FACE",FACE,{"disambiguationData":[OSD([sQuery(id+"F4.wireOp",EDGE,"E10.sketch_text.stroke-36")])]});
            var Q151;
            Q151=makeQuery(id+"F5.opExtrude","SWEPT_FACE",FACE,{"disambiguationData":[OSD([sQuery(id+"F4.wireOp",EDGE,"E10.sketch_text.stroke-22")])]});
            var Q152;
            Q152=makeQuery(id+"F5.boolean.opBoolean","SPLIT",FACE,{"disambiguationData":[TD([makeQuery(id+"F5.opExtrude","SWEPT_FACE",FACE,{"disambiguationData":[OSD([sQuery(id+"F4.wireOp",EDGE,"E10.sketch_text.stroke-119")])]})])],"derivedFrom":makeQuery(id+"F1.opExtrude","CAP_FACE",FACE,{"disambiguationData":[OSD([sQuery(id+"F0.wireOp",EDGE,"E0.bottom"),sQuery(id+"F0.wireOp",EDGE,"E0.top"),sQuery(id+"F0.wireOp",EDGE,"E0.left"),sQuery(id+"F0.wireOp",EDGE,"E0.right"),sQuery(id+"F0.wireOp",EDGE,"E1"),sQuery(id+"F0.wireOp",EDGE,"E7.MirrorC"),sQuery(id+"F0.wireOp",EDGE,"E8.MirrorC"),sQuery(id+"F0.wireOp",EDGE,"E9.MirrorC")])],"isStart":true})});
            var Q153;
            Q153=makeQuery(id+"F5.boolean.opBoolean","SPLIT",FACE,{"disambiguationData":[TD([makeQuery(id+"F5.opExtrude","SWEPT_FACE",FACE,{"disambiguationData":[OSD([sQuery(id+"F4.wireOp",EDGE,"E10.sketch_text.stroke-158")])]})])],"derivedFrom":makeQuery(id+"F1.opExtrude","CAP_FACE",FACE,{"disambiguationData":[OSD([sQuery(id+"F0.wireOp",EDGE,"E0.bottom"),sQuery(id+"F0.wireOp",EDGE,"E0.top"),sQuery(id+"F0.wireOp",EDGE,"E0.left"),sQuery(id+"F0.wireOp",EDGE,"E0.right"),sQuery(id+"F0.wireOp",EDGE,"E1"),sQuery(id+"F0.wireOp",EDGE,"E7.MirrorC"),sQuery(id+"F0.wireOp",EDGE,"E8.MirrorC"),sQuery(id+"F0.wireOp",EDGE,"E9.MirrorC")])],"isStart":true})});
            var Q154;
            Q154=makeQuery(id+"F5.opExtrude","SWEPT_FACE",FACE,{"disambiguationData":[OSD([sQuery(id+"F4.wireOp",EDGE,"E10.sketch_text.stroke-9")])]});
            var Q155;
            Q155=makeQuery(id+"F5.opExtrude","SWEPT_FACE",FACE,{"disambiguationData":[OSD([sQuery(id+"F4.wireOp",EDGE,"E10.sketch_text.stroke-167")])]});
            var Q156;
            Q156=makeQuery(id+"F5.opExtrude","SWEPT_FACE",FACE,{"disambiguationData":[OSD([sQuery(id+"F4.wireOp",EDGE,"E10.sketch_text.stroke-95")])]});
            var Q157;
            Q157=makeQuery(id+"F5.opExtrude","SWEPT_FACE",FACE,{"disambiguationData":[OSD([sQuery(id+"F4.wireOp",EDGE,"E10.sketch_text.stroke-184")])]});
            var Q158;
            Q158=makeQuery(id+"F5.opExtrude","SWEPT_FACE",FACE,{"disambiguationData":[OSD([sQuery(id+"F4.wireOp",EDGE,"E10.sketch_text.stroke-84")])]});
            var Q159;
            Q159=makeQuery(id+"F5.opExtrude","SWEPT_FACE",FACE,{"disambiguationData":[OSD([sQuery(id+"F4.wireOp",EDGE,"E10.sketch_text.stroke-68")])]});
            var Q160;
            Q160=makeQuery(id+"F5.opExtrude","SWEPT_FACE",FACE,{"disambiguationData":[OSD([sQuery(id+"F4.wireOp",EDGE,"E10.sketch_text.stroke-143")])]});
            var Q161;
            Q161=makeQuery(id+"F5.opExtrude","SWEPT_FACE",FACE,{"disambiguationData":[OSD([sQuery(id+"F4.wireOp",EDGE,"E10.sketch_text.stroke-189")])]});
            var Q162;
            Q162=makeQuery(id+"F5.opExtrude","CAP_FACE",FACE,{"disambiguationData":[OSD([sQuery(id+"F4.wireOp",EDGE,"E10.sketch_text.stroke-13"),sQuery(id+"F4.wireOp",EDGE,"E10.sketch_text.stroke-14"),sQuery(id+"F4.wireOp",EDGE,"E10.sketch_text.stroke-15"),sQuery(id+"F4.wireOp",EDGE,"E10.sketch_text.stroke-16"),sQuery(id+"F4.wireOp",EDGE,"E10.sketch_text.stroke-17"),sQuery(id+"F4.wireOp",EDGE,"E10.sketch_text.stroke-18"),sQuery(id+"F4.wireOp",EDGE,"E10.sketch_text.stroke-19"),sQuery(id+"F4.wireOp",EDGE,"E10.sketch_text.stroke-20")])],"isStart":false});
            var Q163;
            Q163=makeQuery(id+"F5.opExtrude","SWEPT_FACE",FACE,{"disambiguationData":[OSD([sQuery(id+"F4.wireOp",EDGE,"E10.sketch_text.stroke-57")])]});
            var Q164;
            Q164=makeQuery(id+"F5.opExtrude","SWEPT_FACE",FACE,{"disambiguationData":[OSD([sQuery(id+"F4.wireOp",EDGE,"E10.sketch_text.stroke-29")])]});
            var Q165;
            Q165=makeQuery(id+"F5.opExtrude","SWEPT_FACE",FACE,{"disambiguationData":[OSD([sQuery(id+"F4.wireOp",EDGE,"E10.sketch_text.stroke-60")])]});
            var Q166;
            Q166=makeQuery(id+"F5.opExtrude","SWEPT_FACE",FACE,{"disambiguationData":[OSD([sQuery(id+"F4.wireOp",EDGE,"E10.sketch_text.stroke-148")])]});
            var Q167;
            Q167=makeQuery(id+"F5.opExtrude","SWEPT_FACE",FACE,{"disambiguationData":[OSD([sQuery(id+"F4.wireOp",EDGE,"E10.sketch_text.stroke-75")])]});
            var Q168;
            Q168=makeQuery(id+"F5.opExtrude","SWEPT_FACE",FACE,{"disambiguationData":[OSD([sQuery(id+"F4.wireOp",EDGE,"E10.sketch_text.stroke-91")])]});
            var Q169;
            Q169=makeQuery(id+"F5.opExtrude","SWEPT_FACE",FACE,{"disambiguationData":[OSD([sQuery(id+"F4.wireOp",EDGE,"E10.sketch_text.stroke-78")])]});
            var Q170;
            Q170=makeQuery(id+"F5.opExtrude","SWEPT_FACE",FACE,{"disambiguationData":[OSD([sQuery(id+"F4.wireOp",EDGE,"E10.sketch_text.stroke-62")])]});
            var Q171;
            Q171=makeQuery(id+"F5.opExtrude","SWEPT_FACE",FACE,{"disambiguationData":[OSD([sQuery(id+"F4.wireOp",EDGE,"E10.sketch_text.stroke-182")])]});
            var Q172;
            Q172=makeQuery(id+"F5.opExtrude","SWEPT_FACE",FACE,{"disambiguationData":[OSD([sQuery(id+"F4.wireOp",EDGE,"E10.sketch_text.stroke-11")])]});
            var Q173;
            Q173=makeQuery(id+"F5.opExtrude","SWEPT_FACE",FACE,{"disambiguationData":[OSD([sQuery(id+"F4.wireOp",EDGE,"E10.sketch_text.stroke-97")])]});
            var Q174;
            Q174=makeQuery(id+"F5.opExtrude","SWEPT_FACE",FACE,{"disambiguationData":[OSD([sQuery(id+"F4.wireOp",EDGE,"E10.sketch_text.stroke-23")])]});
            var Q175;
            Q175=makeQuery(id+"F5.opExtrude","SWEPT_FACE",FACE,{"disambiguationData":[OSD([sQuery(id+"F4.wireOp",EDGE,"E10.sketch_text.stroke-80")])]});
            var Q176;
            Q176=makeQuery(id+"F5.boolean.opBoolean","SPLIT",FACE,{"disambiguationData":[TD([makeQuery(id+"F5.opExtrude","SWEPT_FACE",FACE,{"disambiguationData":[OSD([sQuery(id+"F4.wireOp",EDGE,"E10.sketch_text.stroke-99")])]})])],"derivedFrom":makeQuery(id+"F1.opExtrude","CAP_FACE",FACE,{"disambiguationData":[OSD([sQuery(id+"F0.wireOp",EDGE,"E0.bottom"),sQuery(id+"F0.wireOp",EDGE,"E0.top"),sQuery(id+"F0.wireOp",EDGE,"E0.left"),sQuery(id+"F0.wireOp",EDGE,"E0.right"),sQuery(id+"F0.wireOp",EDGE,"E1"),sQuery(id+"F0.wireOp",EDGE,"E7.MirrorC"),sQuery(id+"F0.wireOp",EDGE,"E8.MirrorC"),sQuery(id+"F0.wireOp",EDGE,"E9.MirrorC")])],"isStart":true})});
            var Q177;
            Q177=makeQuery(id+"F5.opExtrude","SWEPT_FACE",FACE,{"disambiguationData":[OSD([sQuery(id+"F4.wireOp",EDGE,"E10.sketch_text.stroke-168")])]});
            var Q178;
            Q178=makeQuery(id+"F5.opExtrude","SWEPT_FACE",FACE,{"disambiguationData":[OSD([sQuery(id+"F4.wireOp",EDGE,"E10.sketch_text.stroke-188")])]});
            var Q179;
            Q179=makeQuery(id+"F5.opExtrude","SWEPT_FACE",FACE,{"disambiguationData":[OSD([sQuery(id+"F4.wireOp",EDGE,"E10.sketch_text.stroke-129")])]});
            var Q180;
            Q180=makeQuery(id+"F5.opExtrude","SWEPT_FACE",FACE,{"disambiguationData":[OSD([sQuery(id+"F4.wireOp",EDGE,"E10.sketch_text.stroke-27")])]});
            var Q181;
            Q181=makeQuery(id+"F5.opExtrude","SWEPT_FACE",FACE,{"disambiguationData":[OSD([sQuery(id+"F4.wireOp",EDGE,"E10.sketch_text.stroke-175")])]});
            var Q182;
            Q182=makeQuery(id+"F5.opExtrude","SWEPT_FACE",FACE,{"disambiguationData":[OSD([sQuery(id+"F4.wireOp",EDGE,"E10.sketch_text.stroke-42")])]});
            var Q183;
            Q183=makeQuery(id+"F5.opExtrude","SWEPT_FACE",FACE,{"disambiguationData":[OSD([sQuery(id+"F4.wireOp",EDGE,"E10.sketch_text.stroke-118")])]});
            var Q184;
            Q184=makeQuery(id+"F5.opExtrude","SWEPT_FACE",FACE,{"disambiguationData":[OSD([sQuery(id+"F4.wireOp",EDGE,"E10.sketch_text.stroke-151")])]});
            var Q185;
            Q185=makeQuery(id+"F5.opExtrude","SWEPT_FACE",FACE,{"disambiguationData":[OSD([sQuery(id+"F4.wireOp",EDGE,"E10.sketch_text.stroke-137")])]});
            var Q186;
            Q186=makeQuery(id+"F5.opExtrude","SWEPT_FACE",FACE,{"disambiguationData":[OSD([sQuery(id+"F4.wireOp",EDGE,"E10.sketch_text.stroke-83")])]});
            var Q187;
            Q187=makeQuery(id+"F5.boolean.opBoolean","SPLIT",FACE,{"disambiguationData":[TD([makeQuery(id+"F5.opExtrude","SWEPT_FACE",FACE,{"disambiguationData":[OSD([sQuery(id+"F4.wireOp",EDGE,"E10.sketch_text.stroke-90")])]})])],"derivedFrom":makeQuery(id+"F1.opExtrude","CAP_FACE",FACE,{"disambiguationData":[OSD([sQuery(id+"F0.wireOp",EDGE,"E0.bottom"),sQuery(id+"F0.wireOp",EDGE,"E0.top"),sQuery(id+"F0.wireOp",EDGE,"E0.left"),sQuery(id+"F0.wireOp",EDGE,"E0.right"),sQuery(id+"F0.wireOp",EDGE,"E1"),sQuery(id+"F0.wireOp",EDGE,"E7.MirrorC"),sQuery(id+"F0.wireOp",EDGE,"E8.MirrorC"),sQuery(id+"F0.wireOp",EDGE,"E9.MirrorC")])],"isStart":true})});
            var Q188;
            Q188=makeQuery(id+"F5.opExtrude","SWEPT_FACE",FACE,{"disambiguationData":[OSD([sQuery(id+"F4.wireOp",EDGE,"E10.sketch_text.stroke-139")])]});
            var Q189;
            Q189=makeQuery(id+"F5.opExtrude","SWEPT_FACE",FACE,{"disambiguationData":[OSD([sQuery(id+"F4.wireOp",EDGE,"E10.sketch_text.stroke-70")])]});
            var Q190;
            Q190=makeQuery(id+"F5.opExtrude","SWEPT_FACE",FACE,{"disambiguationData":[OSD([sQuery(id+"F4.wireOp",EDGE,"E10.sketch_text.stroke-160")])]});
            var Q191;
            Q191=makeQuery(id+"F5.opExtrude","SWEPT_FACE",FACE,{"disambiguationData":[OSD([sQuery(id+"F4.wireOp",EDGE,"E10.sketch_text.stroke-71")])]});
            var Q192;
            Q192=makeQuery(id+"F5.opExtrude","SWEPT_FACE",FACE,{"disambiguationData":[OSD([sQuery(id+"F4.wireOp",EDGE,"E10.sketch_text.stroke-117")])]});
            var Q193;
            Q193=makeQuery(id+"F5.opExtrude","SWEPT_FACE",FACE,{"disambiguationData":[OSD([sQuery(id+"F4.wireOp",EDGE,"E10.sketch_text.stroke-147")])]});
            var Q194;
            Q194=makeQuery(id+"F5.opExtrude","SWEPT_FACE",FACE,{"disambiguationData":[OSD([sQuery(id+"F4.wireOp",EDGE,"E10.sketch_text.stroke-164")])]});
            var Q195;
            Q195=makeQuery(id+"F5.opExtrude","SWEPT_FACE",FACE,{"disambiguationData":[OSD([sQuery(id+"F4.wireOp",EDGE,"E10.sketch_text.stroke-61")])]});
            var Q196;
            Q196=makeQuery(id+"F5.opExtrude","SWEPT_FACE",FACE,{"disambiguationData":[OSD([sQuery(id+"F4.wireOp",EDGE,"E10.sketch_text.stroke-19")])]});
            var Q197;
            Q197=makeQuery(id+"F5.opExtrude","SWEPT_FACE",FACE,{"disambiguationData":[OSD([sQuery(id+"F4.wireOp",EDGE,"E10.sketch_text.stroke-35")])]});
            var Q198;
            Q198=makeQuery(id+"F5.opExtrude","SWEPT_FACE",FACE,{"disambiguationData":[OSD([sQuery(id+"F4.wireOp",EDGE,"E10.sketch_text.stroke-140")])]});
            var Q199;
            Q199=makeQuery(id+"F5.opExtrude","SWEPT_FACE",FACE,{"disambiguationData":[OSD([sQuery(id+"F4.wireOp",EDGE,"E10.sketch_text.stroke-20")])]});
            var Q200;
            Q200=makeQuery(id+"F5.opExtrude","SWEPT_FACE",FACE,{"disambiguationData":[OSD([sQuery(id+"F4.wireOp",EDGE,"E10.sketch_text.stroke-16")])]});
            var Q201;
            Q201=makeQuery(id+"F5.opExtrude","SWEPT_FACE",FACE,{"disambiguationData":[OSD([sQuery(id+"F4.wireOp",EDGE,"E10.sketch_text.stroke-18")])]});
            var Q202;
            Q202=makeQuery(id+"F5.opExtrude","SWEPT_FACE",FACE,{"disambiguationData":[OSD([sQuery(id+"F4.wireOp",EDGE,"E10.sketch_text.stroke-17")])]});
            var Q203;
            Q203=qCreatedBy(makeId("Right.planeOp"),FACE);
            mirror(context, id + "F6", {"operationType" : NewBodyOperationType.ADD, "entities" : qUnion([Q0]), "faces" : qUnion([Q1, Q2, Q3, Q4, Q5, Q6, Q7, Q8, Q9, Q10, Q11, Q12, Q13, Q14, Q15, Q16, Q17, Q18, Q19, Q20, Q21, Q22, Q23, Q24, Q25, Q26, Q27, Q28, Q29, Q30, Q31, Q32, Q33, Q34, Q35, Q36, Q37, Q38, Q39, Q40, Q41, Q42, Q43, Q44, Q45, Q46, Q47, Q48, Q49, Q50, Q51, Q52, Q53, Q54, Q55, Q56, Q57, Q58, Q59, Q60, Q61, Q62, Q63, Q64, Q65, Q66, Q67, Q68, Q69, Q70, Q71, Q72, Q73, Q74, Q75, Q76, Q77, Q78, Q79, Q80, Q81, Q82, Q83, Q84, Q85, Q86, Q87, Q88, Q89, Q90, Q91, Q92, Q93, Q94, Q95, Q96, Q97, Q98, Q99, Q100, Q101, Q102, Q103, Q104, Q105, Q106, Q107, Q108, Q109, Q110, Q111, Q112, Q113, Q114, Q115, Q116, Q117, Q118, Q119, Q120, Q121, Q122, Q123, Q124, Q125, Q126, Q127, Q128, Q129, Q130, Q131, Q132, Q133, Q134, Q135, Q136, Q137, Q138, Q139, Q140, Q141, Q142, Q143, Q144, Q145, Q146, Q147, Q148, Q149, Q150, Q151, Q152, Q153, Q154, Q155, Q156, Q157, Q158, Q159, Q160, Q161, Q162, Q163, Q164, Q165, Q166, Q167, Q168, Q169, Q170, Q171, Q172, Q173, Q174, Q175, Q176, Q177, Q178, Q179, Q180, Q181, Q182, Q183, Q184, Q185, Q186, Q187, Q188, Q189, Q190, Q191, Q192, Q193, Q194, Q195, Q196, Q197, Q198, Q199, Q200, Q201, Q202]), "mirrorPlane" : qUnion([Q203])});
        }
    });
